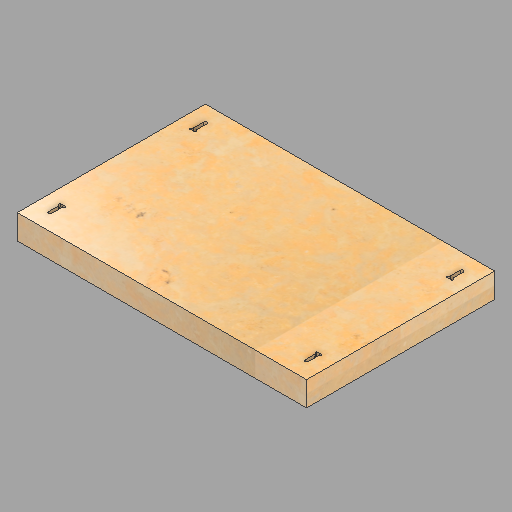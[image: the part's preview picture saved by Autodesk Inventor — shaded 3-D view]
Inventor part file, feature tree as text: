
AUTODESK INVENTOR PART (.ipt)
format: ipt  version: 2023 (Build 270158000, 158)  size: 483,840 bytes
history: native  units: in
note: dims shown in document units (in); Inventor stores cm internally (conversion verified against a paired STEP export)
features: other x14, revolve x6, sketch x4, extrude x1, plane x1, split x1, move_body x1, boolean_combine x1, projected_geometry x1
ambient origin geometry x8: Origin, YZ Plane, XZ Plane, XY Plane, X Axis, Y Axis, Z Axis, Center Point
bodies: Solid1 (feature_tree), Solid2 (feature_tree), Solid3 (feature_tree)
feature tree (30):
  other  "Blocks"
  extrude  "Extrusion1"  Depth=23.0in
  sketch  "Sketch2"  dims[d2=47.375in d3=0.0in d4=2.0in]
  revolve  "Revolution1"  [1 undecoded]
  revolve  "Revolution2"  Angle=90.0deg
  sketch  "Sketch3"  dims[d5=1.0in d6=90.0deg]
  revolve  "Revolution3"  Angle=90.0deg
  revolve  "Revolution4"  Angle=90.0deg
  sketch  "Sketch4"  dims[d7=90.0deg d8=90.0deg d9=90.0deg d10=90.0deg d11=90.0deg d12=-12.0in d13=0.0in d14=0.0in]
  revolve  "Revolution5"  Angle=90.0deg
  revolve  "Revolution6"  Angle=90.0deg
  plane  "Work Plane1"
  split  "Split1"
  move_body  "Move Body1"
  boolean_combine  "Combine1"
  sketch  "Sketch1"  dims[d0=2.0in d1=23.0in]
  projected_geometry  "Projected Loop1"
  other  "Bolt"
  other  "Block2"
  other  "Block3"
  other  "Block2:1"
  other  "Bolt:2"
  other  "Block2:2"
  other  "Block2:4"
  other  "Block3:1"
  other  "Block3:2"
  other  "Block3:3"
  other  "Block3:4"
  other  "Block3:5"
  other  "Block3:6"
note: 1 required parameter value undecoded (feature->parameter linkage not recoverable at this tier; creation-order binding heuristic only, values carry confidence <= 0.55)
